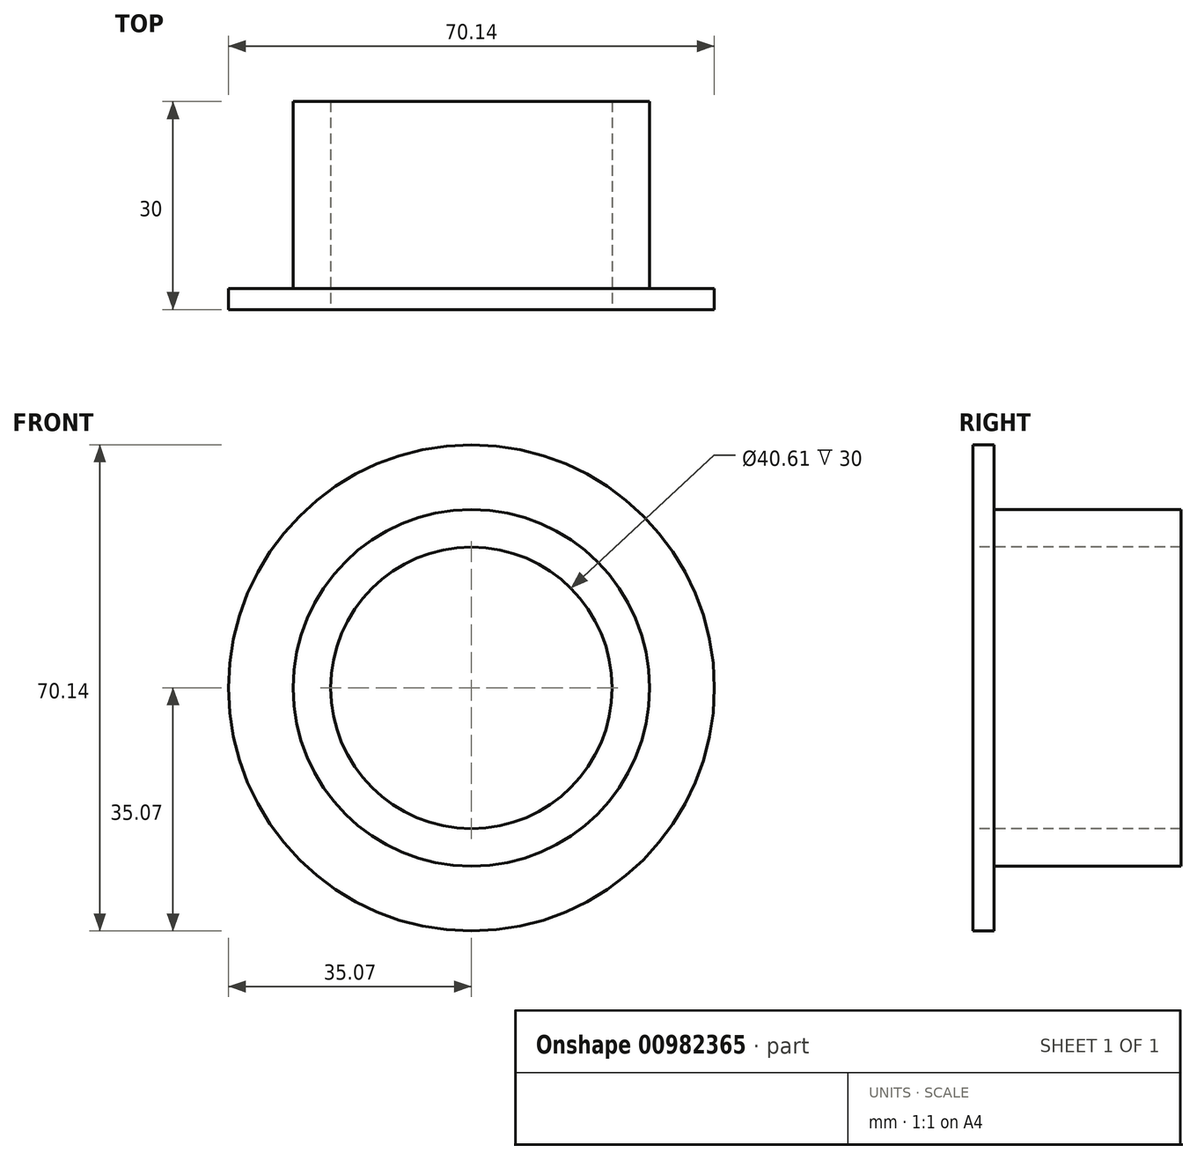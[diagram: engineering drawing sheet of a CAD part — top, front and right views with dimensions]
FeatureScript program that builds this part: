
annotation { "Feature Type Name" : "Feature", "Feature Type Description" : "" }
export const myFeature = defineFeature(function(context is Context, id is Id, definition is map)
    precondition{}
    {
        {
            var Q0;
            Q0=qCreatedBy(makeId("Front.planeOp"),FACE);
            var sketch = newSketch(context, id + "F0", { "sketchPlane" : qUnion([Q0])});
            skCircle(sketch, "E0", {"center": v(0, 0) * mm, "radius": 20.25 * mm});
            skCircle(sketch, "E1", {"center": v(0, 0) * mm, "radius": 25.75 * mm});
            skCircle(sketch, "E2", {"center": v(0, 0) * mm, "radius": 35 * mm});
            skSolve(sketch);
        }
        {
            var Q0;
            Q0=qCreatedBy(makeId("Right.planeOp"),FACE);
            var sketch = newSketch(context, id + "F1", { "sketchPlane" : qUnion([Q0])});
            skPoint(sketch, "E3.middle", {"position": v(0, 0) * mm});
            skLineSegment(sketch, "E4.bottom", {"start": v(0, -20.3) * mm, "end": v(0, -20.3) * mm});
            skLineSegment(sketch, "E5.bottom", {"start": v(30, -25.73) * mm, "end": v(3, -25.73) * mm});
            skLineSegment(sketch, "E5.top", {"start": v(30, -20.3) * mm, "end": v(0, -20.3) * mm});
            skLineSegment(sketch, "E5.left", {"start": v(30, -25.73) * mm, "end": v(30, -20.3) * mm});
            skLineSegment(sketch, "E6.top", {"start": v(0, -35.07) * mm, "end": v(3, -35.07) * mm});
            skLineSegment(sketch, "E6.right", {"start": v(3, -25.73) * mm, "end": v(3, -35.07) * mm});
            skSolve(sketch);
        }
        {
            var Q0;
            Q0 = qSketchRegion(id + "F1", true);
            var Q1;
            Q1=sQuery(id+"F1.wireOp",EDGE,"E5.top");
            var Q2;
            Q2=sQuery(id+"F1.wireOp",EDGE,"E5.left");
            var Q3;
            Q3=sQuery(id+"F1.wireOp",EDGE,"E5.bottom");
            var Q4;
            Q4=sQuery(id+"F1.wireOp",EDGE,"E6.right");
            var Q5;
            Q5=sQuery(id+"F1.wireOp",EDGE,"E6.top");
            var Q6;
            Q6=sQuery(id+"F0.wireOp",EDGE,"E2");
            revolve(context, id + "F2", {"bodyType" : ToolBodyType.SURFACE, "surfaceOperationType" : NewSurfaceOperationType.NEW, "entities" : qUnion([Q0]), "surfaceEntities" : qUnion([Q1, Q2, Q3, Q4, Q5]), "axis" : qUnion([Q6]), "revolveType" : RevolveType.FULL});
        }
    });
